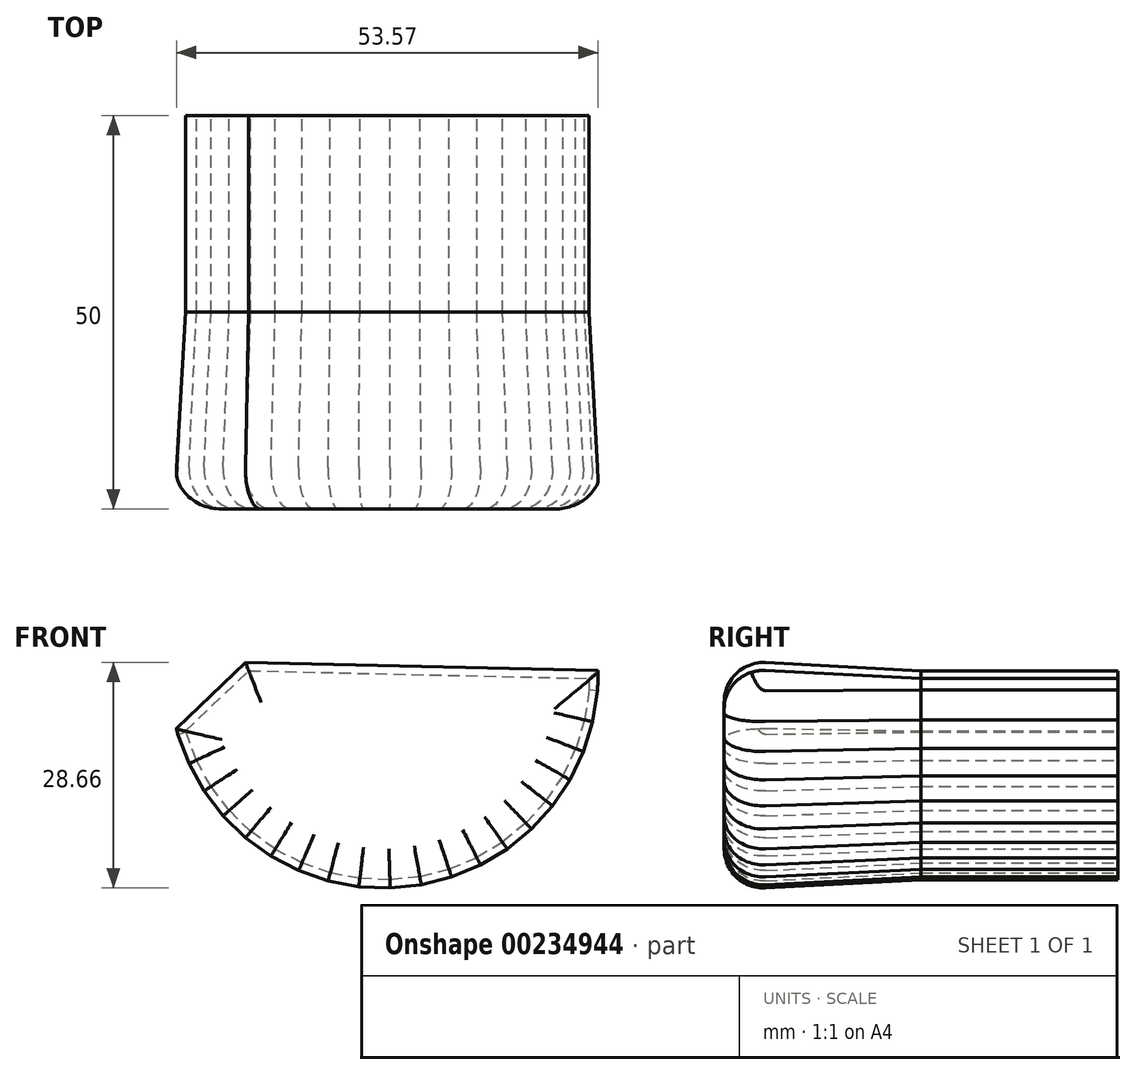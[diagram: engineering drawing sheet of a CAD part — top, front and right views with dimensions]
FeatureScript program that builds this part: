
annotation { "Feature Type Name" : "Feature", "Feature Type Description" : "" }
export const myFeature = defineFeature(function(context is Context, id is Id, definition is map)
    precondition{}
    {
        {
            var Q0;
            Q0=qCreatedBy(makeId("Front.planeOp"),FACE);
            var sketch = newSketch(context, id + "F0", { "sketchPlane" : qUnion([Q0])});
            skCircle(sketch, "E0.cCircle", {"center": v(-33.66, 16.56) * mm, "radius": 83.06 * mm, "construction": true});
            skLineSegment(sketch, "E0.0", {"start": v(48.6, -19.72) * mm, "end": v(-1.14, -67.26) * mm});
            skLineSegment(sketch, "E0.1", {"start": v(-1.14, -67.26) * mm, "end": v(-69.93, -65.7) * mm});
            skLineSegment(sketch, "E0.2", {"start": v(-69.93, -65.7) * mm, "end": v(-117.48, -15.96) * mm});
            skLineSegment(sketch, "E0.3", {"start": v(-117.48, -15.96) * mm, "end": v(-115.92, 52.83) * mm});
            skLineSegment(sketch, "E0.4", {"start": v(-115.92, 52.83) * mm, "end": v(-66.18, 100.37) * mm});
            skLineSegment(sketch, "E0.5", {"start": v(-66.18, 100.37) * mm, "end": v(2.61, 98.82) * mm});
            skLineSegment(sketch, "E0.6", {"start": v(2.61, 98.82) * mm, "end": v(50.15, 49.07) * mm});
            skLineSegment(sketch, "E0.7", {"start": v(50.15, 49.07) * mm, "end": v(48.6, -19.72) * mm});
            skPoint(sketch, "E0.0.midPoint", {"position": v(23.73, -43.49) * mm});
            skCircle(sketch, "E1.cCircle", {"center": v(-14, 10.18) * mm, "radius": 64.68 * mm, "construction": true});
            skLineSegment(sketch, "E1.0", {"start": v(52.34, 9.64) * mm, "end": v(45.53, -19.1) * mm});
            skLineSegment(sketch, "E1.1", {"start": v(45.53, -19.1) * mm, "end": v(26.94, -42.02) * mm});
            skLineSegment(sketch, "E1.2", {"start": v(26.94, -42.02) * mm, "end": v(0.23, -54.62) * mm});
            skLineSegment(sketch, "E1.3", {"start": v(0.23, -54.62) * mm, "end": v(-29.3, -54.38) * mm});
            skLineSegment(sketch, "E1.4", {"start": v(-29.3, -54.38) * mm, "end": v(-55.79, -41.35) * mm});
            skLineSegment(sketch, "E1.5", {"start": v(-55.79, -41.35) * mm, "end": v(-74, -18.11) * mm});
            skLineSegment(sketch, "E1.6", {"start": v(-74, -18.11) * mm, "end": v(-80.34, 10.72) * mm});
            skLineSegment(sketch, "E1.7", {"start": v(-80.34, 10.72) * mm, "end": v(-73.54, 39.45) * mm});
            skLineSegment(sketch, "E1.8", {"start": v(-73.54, 39.45) * mm, "end": v(-54.94, 62.39) * mm});
            skLineSegment(sketch, "E1.9", {"start": v(-54.94, 62.39) * mm, "end": v(-28.23, 74.98) * mm});
            skLineSegment(sketch, "E1.10", {"start": v(-28.23, 74.98) * mm, "end": v(1.3, 74.74) * mm});
            skLineSegment(sketch, "E1.11", {"start": v(1.3, 74.74) * mm, "end": v(27.79, 61.7) * mm});
            skLineSegment(sketch, "E1.12", {"start": v(27.79, 61.7) * mm, "end": v(46, 38.48) * mm});
            skLineSegment(sketch, "E1.13", {"start": v(46, 38.48) * mm, "end": v(52.34, 9.64) * mm});
            skPoint(sketch, "E1.0.midPoint", {"position": v(48.94, -4.73) * mm});
            skCircle(sketch, "E2.cCircle", {"center": v(-33.66, 7) * mm, "radius": 55.18 * mm, "construction": true});
            skLineSegment(sketch, "E2.0", {"start": v(26.15, 39.76) * mm, "end": v(15.99, -39.76) * mm});
            skLineSegment(sketch, "E2.1", {"start": v(15.99, -39.76) * mm, "end": v(-62.79, -54.68) * mm});
            skLineSegment(sketch, "E2.2", {"start": v(-62.79, -54.68) * mm, "end": v(-101.31, 15.63) * mm});
            skLineSegment(sketch, "E2.3", {"start": v(-101.31, 15.63) * mm, "end": v(-46.35, 74) * mm});
            skLineSegment(sketch, "E2.4", {"start": v(-46.35, 74) * mm, "end": v(26.15, 39.76) * mm});
            skPoint(sketch, "E2.0.midPoint", {"position": v(21.07, 0) * mm});
            skCircle(sketch, "E3.cCircle", {"center": v(-49.05, 99.98) * mm, "radius": 26.12 * mm, "construction": true});
            skLineSegment(sketch, "E3.0", {"start": v(-44.45, 74.2) * mm, "end": v(-48.25, 73.8) * mm});
            skLineSegment(sketch, "E3.1", {"start": v(-48.25, 73.8) * mm, "end": v(-52.07, 73.97) * mm});
            skLineSegment(sketch, "E3.2", {"start": v(-52.07, 73.97) * mm, "end": v(-55.82, 74.69) * mm});
            skLineSegment(sketch, "E3.3", {"start": v(-55.82, 74.69) * mm, "end": v(-59.44, 75.94) * mm});
            skLineSegment(sketch, "E3.4", {"start": v(-59.44, 75.94) * mm, "end": v(-62.83, 77.71) * mm});
            skLineSegment(sketch, "E3.5", {"start": v(-62.83, 77.71) * mm, "end": v(-65.92, 79.95) * mm});
            skLineSegment(sketch, "E3.6", {"start": v(-65.92, 79.95) * mm, "end": v(-68.66, 82.62) * mm});
            skLineSegment(sketch, "E3.7", {"start": v(-68.66, 82.62) * mm, "end": v(-70.98, 85.67) * mm});
            skLineSegment(sketch, "E3.8", {"start": v(-70.98, 85.67) * mm, "end": v(-72.83, 89.01) * mm});
            skLineSegment(sketch, "E3.9", {"start": v(-72.83, 89.01) * mm, "end": v(-74.17, 92.6) * mm});
            skLineSegment(sketch, "E3.10", {"start": v(-74.17, 92.6) * mm, "end": v(-74.98, 96.33) * mm});
            skLineSegment(sketch, "E3.11", {"start": v(-74.98, 96.33) * mm, "end": v(-75.24, 100.14) * mm});
            skLineSegment(sketch, "E3.12", {"start": v(-75.24, 100.14) * mm, "end": v(-74.94, 103.95) * mm});
            skLineSegment(sketch, "E3.13", {"start": v(-74.94, 103.95) * mm, "end": v(-74.08, 107.68) * mm});
            skLineSegment(sketch, "E3.14", {"start": v(-74.08, 107.68) * mm, "end": v(-72.7, 111.24) * mm});
            skLineSegment(sketch, "E3.15", {"start": v(-72.7, 111.24) * mm, "end": v(-70.8, 114.57) * mm});
            skLineSegment(sketch, "E3.16", {"start": v(-70.8, 114.57) * mm, "end": v(-68.45, 117.58) * mm});
            skLineSegment(sketch, "E3.17", {"start": v(-68.45, 117.58) * mm, "end": v(-65.68, 120.22) * mm});
            skLineSegment(sketch, "E3.18", {"start": v(-65.68, 120.22) * mm, "end": v(-62.56, 122.42) * mm});
            skLineSegment(sketch, "E3.19", {"start": v(-62.56, 122.42) * mm, "end": v(-59.14, 124.15) * mm});
            skLineSegment(sketch, "E3.20", {"start": v(-59.14, 124.15) * mm, "end": v(-55.52, 125.36) * mm});
            skLineSegment(sketch, "E3.21", {"start": v(-55.52, 125.36) * mm, "end": v(-51.75, 126.04) * mm});
            skLineSegment(sketch, "E3.22", {"start": v(-51.75, 126.04) * mm, "end": v(-47.93, 126.15) * mm});
            skLineSegment(sketch, "E3.23", {"start": v(-47.93, 126.15) * mm, "end": v(-44.13, 125.71) * mm});
            skLineSegment(sketch, "E3.24", {"start": v(-44.13, 125.71) * mm, "end": v(-40.44, 124.72) * mm});
            skLineSegment(sketch, "E3.25", {"start": v(-40.44, 124.72) * mm, "end": v(-36.93, 123.2) * mm});
            skLineSegment(sketch, "E3.26", {"start": v(-36.93, 123.2) * mm, "end": v(-33.68, 121.2) * mm});
            skLineSegment(sketch, "E3.27", {"start": v(-33.68, 121.2) * mm, "end": v(-30.75, 118.73) * mm});
            skLineSegment(sketch, "E3.28", {"start": v(-30.75, 118.73) * mm, "end": v(-28.22, 115.87) * mm});
            skLineSegment(sketch, "E3.29", {"start": v(-28.22, 115.87) * mm, "end": v(-26.13, 112.66) * mm});
            skLineSegment(sketch, "E3.30", {"start": v(-26.13, 112.66) * mm, "end": v(-24.53, 109.2) * mm});
            skLineSegment(sketch, "E3.31", {"start": v(-24.53, 109.2) * mm, "end": v(-23.45, 105.52) * mm});
            skLineSegment(sketch, "E3.32", {"start": v(-23.45, 105.52) * mm, "end": v(-22.91, 101.74) * mm});
            skLineSegment(sketch, "E3.33", {"start": v(-22.91, 101.74) * mm, "end": v(-22.94, 97.91) * mm});
            skLineSegment(sketch, "E3.34", {"start": v(-22.94, 97.91) * mm, "end": v(-23.52, 94.13) * mm});
            skLineSegment(sketch, "E3.35", {"start": v(-23.52, 94.13) * mm, "end": v(-24.64, 90.48) * mm});
            skLineSegment(sketch, "E3.36", {"start": v(-24.64, 90.48) * mm, "end": v(-26.28, 87.03) * mm});
            skLineSegment(sketch, "E3.37", {"start": v(-26.28, 87.03) * mm, "end": v(-28.41, 83.85) * mm});
            skLineSegment(sketch, "E3.38", {"start": v(-28.41, 83.85) * mm, "end": v(-30.98, 81.02) * mm});
            skLineSegment(sketch, "E3.39", {"start": v(-30.98, 81.02) * mm, "end": v(-33.94, 78.6) * mm});
            skLineSegment(sketch, "E3.40", {"start": v(-33.94, 78.6) * mm, "end": v(-37.21, 76.62) * mm});
            skLineSegment(sketch, "E3.41", {"start": v(-37.21, 76.62) * mm, "end": v(-40.74, 75.14) * mm});
            skLineSegment(sketch, "E3.42", {"start": v(-40.74, 75.14) * mm, "end": v(-44.45, 74.2) * mm});
            skPoint(sketch, "E3.0.midPoint", {"position": v(-46.35, 74) * mm});
            skSolve(sketch);
        }
        {
            var Q0;
            {var subQ7=sQuery(id+"F0.wireOp",EDGE,"E3.1");Q0=makeQuery(id+"F0.imprint","IMPRINT",FACE,{"disambiguationData":[TD([[makeQuery(id+"F0.imprint","IMPRINT",EDGE,{"derivedFrom":subQ7}),-1.0]])]});}
            extrude(context, id + "F1", {"entities" : qUnion([Q0]), "depth" : 25 * mm, "hasDraft" : true, "draftAngle" : 3 * degree, "hasSecondDirection" : true, "secondDirectionOppositeDirection" : true, "secondDirectionDepth" : 25 * mm});
        }
        {
            var Q0;
            Q0=makeQuery(id+"F1.opExtrude","CAP_FACE",FACE,{"disambiguationData":[OSD([sQuery(id+"F0.wireOp",EDGE,"E0.4"),sQuery(id+"F0.wireOp",EDGE,"E0.5"),sQuery(id+"F0.wireOp",EDGE,"E3.0"),sQuery(id+"F0.wireOp",EDGE,"E3.1"),sQuery(id+"F0.wireOp",EDGE,"E3.2"),sQuery(id+"F0.wireOp",EDGE,"E3.3"),sQuery(id+"F0.wireOp",EDGE,"E3.4"),sQuery(id+"F0.wireOp",EDGE,"E3.5"),sQuery(id+"F0.wireOp",EDGE,"E3.6"),sQuery(id+"F0.wireOp",EDGE,"E3.7"),sQuery(id+"F0.wireOp",EDGE,"E3.8"),sQuery(id+"F0.wireOp",EDGE,"E3.9"),sQuery(id+"F0.wireOp",EDGE,"E3.10"),sQuery(id+"F0.wireOp",EDGE,"E3.33"),sQuery(id+"F0.wireOp",EDGE,"E3.34"),sQuery(id+"F0.wireOp",EDGE,"E3.35"),sQuery(id+"F0.wireOp",EDGE,"E3.36"),sQuery(id+"F0.wireOp",EDGE,"E3.37"),sQuery(id+"F0.wireOp",EDGE,"E3.38"),sQuery(id+"F0.wireOp",EDGE,"E3.39"),sQuery(id+"F0.wireOp",EDGE,"E3.40"),sQuery(id+"F0.wireOp",EDGE,"E3.41"),sQuery(id+"F0.wireOp",EDGE,"E3.42")])],"isStart":false});
            fillet(context, id + "F2", {"entities" : qUnion([Q0]), "radius" : 5 * mm, "tangentPropagation" : true, "allowEdgeOverflow" : false});
        }
    });
